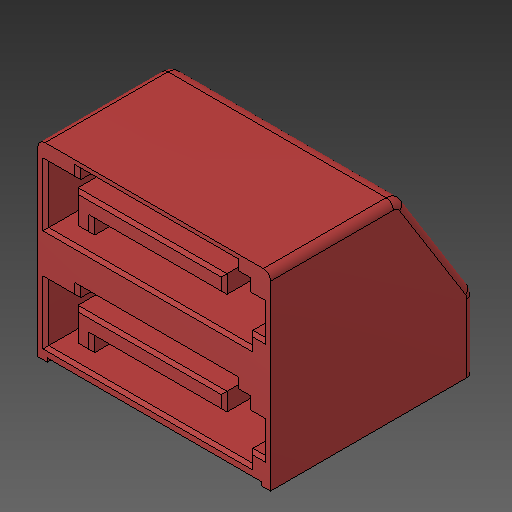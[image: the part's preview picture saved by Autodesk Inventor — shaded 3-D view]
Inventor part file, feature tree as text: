
AUTODESK INVENTOR PART (.ipt)
format: ipt  version: 2018.2 (Build 222227000, 227)  size: 155,648 bytes
history: native  units: mm
features: other x1, fillet x1
ambient origin geometry x8: Origin, YZ Plane, XZ Plane, XY Plane, X Axis, Y Axis, Z Axis, Center Point
bodies: Body1 (feature_tree)
feature tree (2):
  other  "ソリッド1"
  fillet  "Fillet2"  [1 undecoded]
note: 1 required parameter value undecoded (feature->parameter linkage not recoverable at this tier; creation-order binding heuristic only, values carry confidence <= 0.55)
